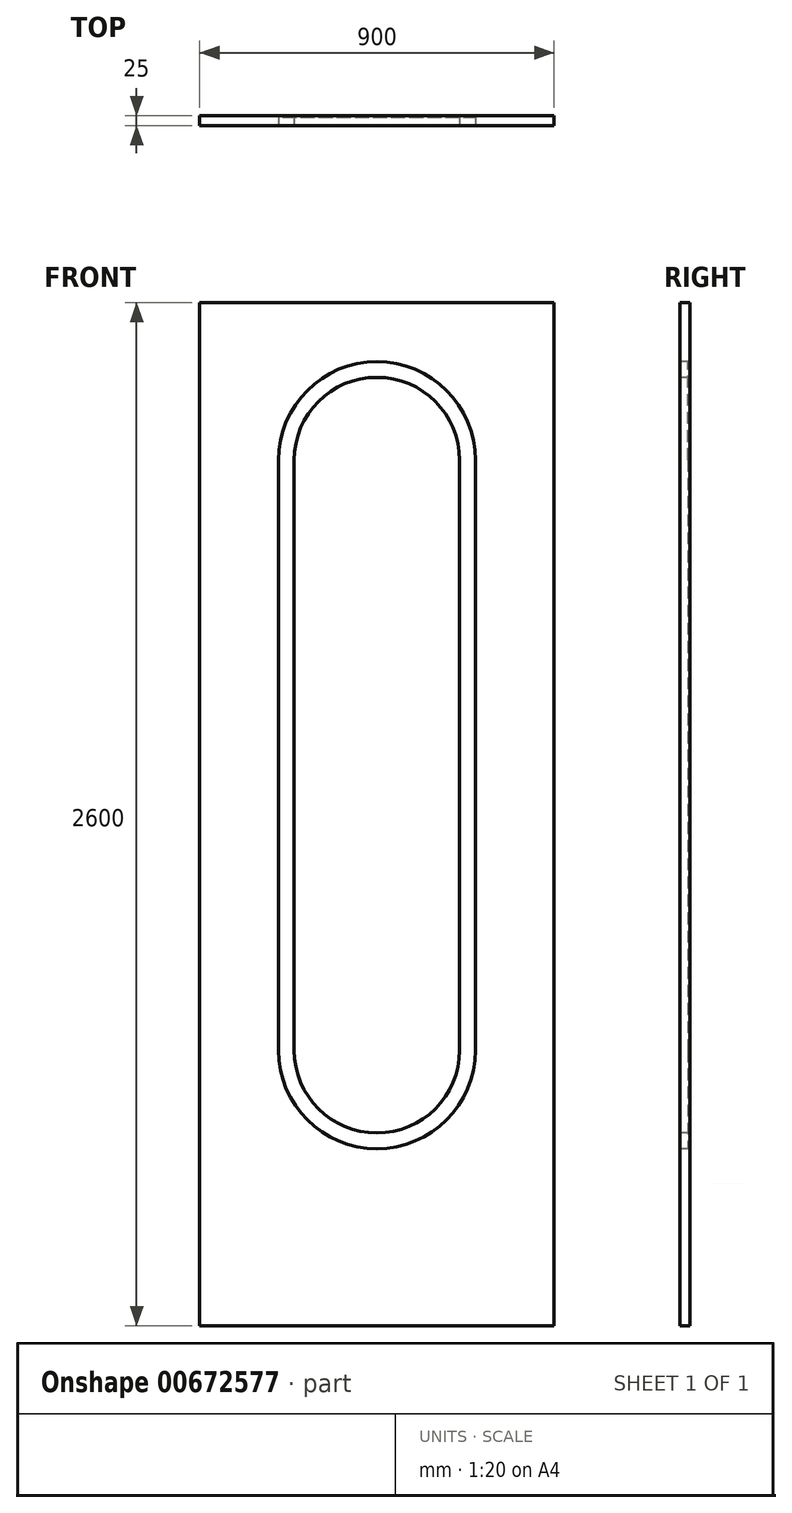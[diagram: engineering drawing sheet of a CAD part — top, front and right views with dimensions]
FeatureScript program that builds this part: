
annotation { "Feature Type Name" : "Feature", "Feature Type Description" : "" }
export const myFeature = defineFeature(function(context is Context, id is Id, definition is map)
    precondition{}
    {
        {
            var Q0;
            Q0=qCreatedBy(makeId("Front.planeOp"),FACE);
            var sketch = newSketch(context, id + "F0", { "sketchPlane" : qUnion([Q0])});
            skLineSegment(sketch, "E0.bottom", {"start": v(-450, 1300) * mm, "end": v(450, 1300) * mm});
            skLineSegment(sketch, "E0.top", {"start": v(-450, -1300) * mm, "end": v(450, -1300) * mm});
            skLineSegment(sketch, "E0.left", {"start": v(-450, 1300) * mm, "end": v(-450, -1300) * mm});
            skLineSegment(sketch, "E0.right", {"start": v(450, 1300) * mm, "end": v(450, -1300) * mm});
            skPoint(sketch, "E0.middle", {"position": v(0, 0) * mm});
            skSolve(sketch);
        }
        {
            var Q0;
            Q0=makeQuery(id+"F0.imprint","IMPRINT",FACE,{"disambiguationData":[TD([[makeQuery(id+"F0.imprint","IMPRINT",EDGE,{"derivedFrom":sQuery(id+"F0.wireOp",EDGE,"E0.bottom")}),-1.0]])]});
            extrude(context, id + "F1", {"entities" : qUnion([Q0]), "depth" : 25 * mm, "offsetDistance" : 25 * mm});
        }
        {
            var Q0;
            Q0=makeQuery(id+"F1.opExtrude","CAP_FACE",FACE,{"disambiguationData":[OSD([sQuery(id+"F0.wireOp",EDGE,"E0.bottom"),sQuery(id+"F0.wireOp",EDGE,"E0.top"),sQuery(id+"F0.wireOp",EDGE,"E0.left"),sQuery(id+"F0.wireOp",EDGE,"E0.right")])],"isStart":false});
            var sketch = newSketch(context, id + "F2", { "sketchPlane" : qUnion([Q0])});
            skLineSegment(sketch, "E1", {"start": v(-450, 0) * mm, "end": v(450, 0) * mm, "construction": true});
            skLineSegment(sketch, "E2", {"start": v(0, -1300) * mm, "end": v(0, 1300) * mm, "construction": true});
            skArc(sketch, "E3", {"start": v(250, 900) * mm, "mid": v(0, 1150) * mm, "end": v(-250, 900) * mm});
            skArc(sketch, "E4", {"start": v(-250, -600) * mm, "mid": v(0, -850) * mm, "end": v(250, -600) * mm});
            skArc(sketch, "E5", {"start": v(210, 900) * mm, "mid": v(0, 1110) * mm, "end": v(-210, 900) * mm});
            skArc(sketch, "E6", {"start": v(-210, -600) * mm, "mid": v(0, -810) * mm, "end": v(210, -600) * mm});
            skLineSegment(sketch, "E7", {"start": v(-250, 900) * mm, "end": v(-250, -600) * mm});
            skLineSegment(sketch, "E8", {"start": v(250, 900) * mm, "end": v(250, -600) * mm});
            skLineSegment(sketch, "E9", {"start": v(-210, 900) * mm, "end": v(-210, -600) * mm});
            skLineSegment(sketch, "E10", {"start": v(210, -600) * mm, "end": v(210, 900) * mm});
            skSolve(sketch);
        }
        {
            var Q0;
            Q0=makeQuery(id+"F2.imprint","IMPRINT",FACE,{"disambiguationData":[TD([[makeQuery(id+"F2.imprint","IMPRINT",EDGE,{"derivedFrom":sQuery(id+"F2.wireOp",EDGE,"E3")}),1.0]])]});
            extrude(context, id + "F3", {"entities" : qUnion([Q0]), "operationType" : NewBodyOperationType.REMOVE, "oppositeDirection" : true, "depth" : 20 * mm, "offsetDistance" : 25 * mm});
        }
    });
